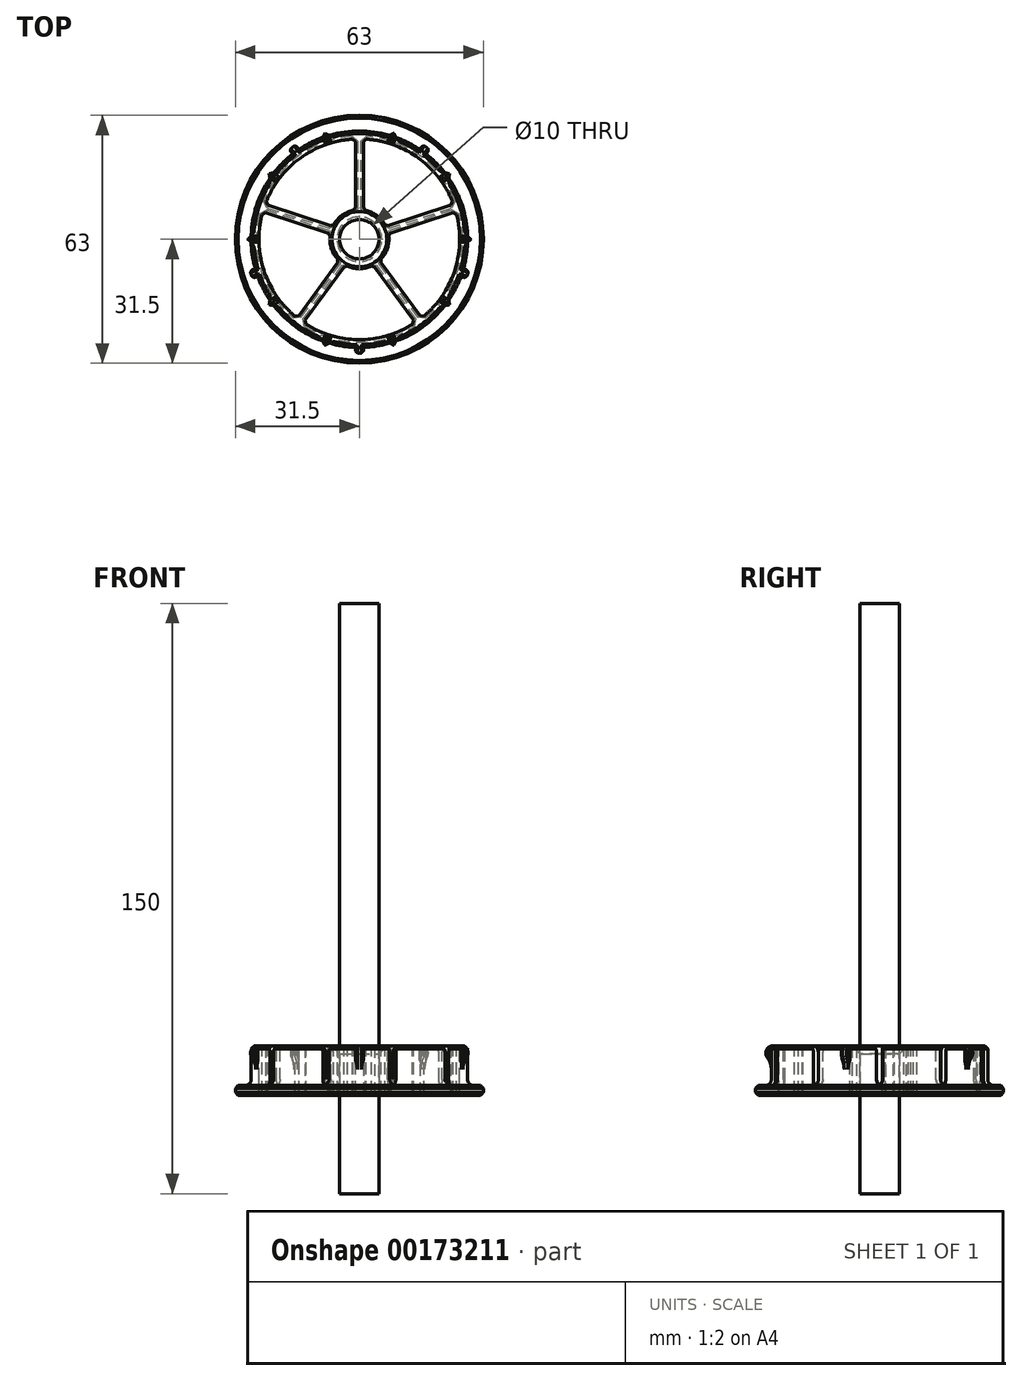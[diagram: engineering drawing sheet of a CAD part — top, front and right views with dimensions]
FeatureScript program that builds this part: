
annotation { "Feature Type Name" : "Feature", "Feature Type Description" : "" }
export const myFeature = defineFeature(function(context is Context, id is Id, definition is map)
    precondition{}
    {
        {
            var Q0;
            Q0=qCreatedBy(makeId("Front.planeOp"),FACE);
            var sketch = newSketch(context, id + "F0", { "sketchPlane" : qUnion([Q0])});
            skLineSegment(sketch, "E0", {"start": v(0, 0) * mm, "end": v(-63, 0) * mm, "construction": true});
            skLineSegment(sketch, "E1", {"start": v(-31.5, 0) * mm, "end": v(-31.5, 2.5) * mm});
            skLineSegment(sketch, "E2", {"start": v(-31.5, 2.5) * mm, "end": v(-27.5, 2.5) * mm});
            skLineSegment(sketch, "E3", {"start": v(-27.5, 2.5) * mm, "end": v(-27.5, 8.9) * mm});
            skLineSegment(sketch, "E4", {"start": v(-31.5, 0) * mm, "end": v(-5, 0) * mm});
            skLineSegment(sketch, "E5", {"start": v(-5, 0) * mm, "end": v(-5, 12.5) * mm});
            skLineSegment(sketch, "E6", {"start": v(-5, 12.5) * mm, "end": v(-27.5, 12.5) * mm});
            skLineSegment(sketch, "E7", {"start": v(0, 0) * mm, "end": v(0, 12.5) * mm, "construction": true});
            skLineSegment(sketch, "E8.0.MirrorCS", {"start": v(5, 0) * mm, "end": v(5, 12.5) * mm});
            skLineSegment(sketch, "E9.0.MirrorCS", {"start": v(5, 12.5) * mm, "end": v(27.5, 12.5) * mm});
            skLineSegment(sketch, "E10.0.MirrorCS", {"start": v(27.5, 2.5) * mm, "end": v(27.5, 12.5) * mm});
            skLineSegment(sketch, "E11.0.MirrorCS", {"start": v(31.5, 0) * mm, "end": v(31.5, 2.5) * mm});
            skLineSegment(sketch, "E12.0.MirrorCS", {"start": v(31.5, 0) * mm, "end": v(5, 0) * mm});
            skLineSegment(sketch, "E13.0.MirrorCS", {"start": v(31.5, 2.5) * mm, "end": v(27.5, 2.5) * mm});
            skArc(sketch, "E14", {"start": v(-27.5, 12.5) * mm, "mid": v(-28.9, 10.7) * mm, "end": v(-27.5, 8.9) * mm});
            skSolve(sketch);
        }
        {
            var Q0;
            Q0=makeQuery(id+"F0.imprint","IMPRINT",FACE,{"disambiguationData":[TD([[makeQuery(id+"F0.imprint","IMPRINT",EDGE,{"derivedFrom":sQuery(id+"F0.wireOp",EDGE,"E1")}),-1.0]])]});
            var Q1;
            Q1=sQuery(id+"F0.wireOp",EDGE,"E7");
            revolve(context, id + "F1", {"entities" : qUnion([Q0]), "axis" : qUnion([Q1]), "revolveType" : RevolveType.FULL});
        }
        {
            var Q0;
            Q0=makeQuery(id+"F1.opRevolve","SWEPT_FACE",FACE,{"disambiguationData":[OSD([sQuery(id+"F0.wireOp",EDGE,"E6")])]});
            var sketch = newSketch(context, id + "F2", { "sketchPlane" : qUnion([Q0])});
            skCircle(sketch, "E15.0", {"center": v(0, 0) * mm, "radius": 31.5 * mm});
            skCircle(sketch, "E15.1", {"center": v(0, 0) * mm, "radius": 5 * mm});
            skCircle(sketch, "E16.0", {"center": v(0, 0) * mm, "radius": 27.5 * mm});
            skCircle(sketch, "E17", {"center": v(0, 0) * mm, "radius": 7.5 * mm});
            skCircle(sketch, "E18", {"center": v(0, 0) * mm, "radius": 25.5 * mm});
            skLineSegment(sketch, "E19", {"start": v(0, 0) * mm, "end": v(0, 31.5) * mm, "construction": true});
            skLineSegment(sketch, "E20", {"start": v(-1, 7.43) * mm, "end": v(-1, 25.48) * mm});
            skLineSegment(sketch, "E21.0.MirrorCS", {"start": v(1, 7.43) * mm, "end": v(1, 25.48) * mm});
            skLineSegment(sketch, "E22.1.0", {"start": v(-7.38, 1.35) * mm, "end": v(-24.54, 6.92) * mm});
            skLineSegment(sketch, "E22.1.1", {"start": v(-6.76, 3.25) * mm, "end": v(-23.92, 8.82) * mm});
            skLineSegment(sketch, "E22.2.0", {"start": v(-3.56, -6.6) * mm, "end": v(-14.17, -21.2) * mm});
            skLineSegment(sketch, "E22.2.1", {"start": v(-5.18, -5.43) * mm, "end": v(-15.79, -20.03) * mm});
            skLineSegment(sketch, "E22.3.0", {"start": v(5.18, -5.43) * mm, "end": v(15.79, -20.03) * mm});
            skLineSegment(sketch, "E22.3.1", {"start": v(3.56, -6.6) * mm, "end": v(14.17, -21.2) * mm});
            skLineSegment(sketch, "E22.4.0", {"start": v(6.76, 3.25) * mm, "end": v(23.92, 8.82) * mm});
            skLineSegment(sketch, "E22.4.1", {"start": v(7.38, 1.35) * mm, "end": v(24.54, 6.92) * mm});
            skLineSegment(sketch, "E23", {"start": v(16.16, 22.25) * mm, "end": v(-16.16, -22.25) * mm, "construction": true});
            skLineSegment(sketch, "E24", {"start": v(15.34, 22.82) * mm, "end": v(17.7, 26.06) * mm});
            skLineSegment(sketch, "E25.0.MirrorCS", {"start": v(16.96, 21.65) * mm, "end": v(19.31, 24.88) * mm});
            skLineSegment(sketch, "E26.1.0", {"start": v(-16.96, 21.65) * mm, "end": v(-19.31, 24.88) * mm});
            skLineSegment(sketch, "E26.1.1", {"start": v(-15.34, 22.82) * mm, "end": v(-17.7, 26.06) * mm});
            skLineSegment(sketch, "E26.2.0", {"start": v(-25.83, -9.44) * mm, "end": v(-29.63, -10.68) * mm});
            skLineSegment(sketch, "E26.2.1", {"start": v(-26.45, -7.54) * mm, "end": v(-30.25, -8.78) * mm});
            skLineSegment(sketch, "E26.3.0", {"start": v(1, -27.48) * mm, "end": v(1, -31.48) * mm});
            skLineSegment(sketch, "E26.3.1", {"start": v(-1, -27.48) * mm, "end": v(-1, -31.48) * mm});
            skLineSegment(sketch, "E26.4.0", {"start": v(26.45, -7.54) * mm, "end": v(30.25, -8.78) * mm});
            skLineSegment(sketch, "E26.4.1", {"start": v(25.83, -9.44) * mm, "end": v(29.63, -10.68) * mm});
            skSolve(sketch);
        }
        {
            var Q0;
            {var subQ10=sQuery(id+"F2.wireOp",EDGE,"E16.0");var subQ16=makeQuery(id+"F2.imprint","INTERSECT",VERTEX,{"derivedFrom":[subQ10,sQuery(id+"F2.wireOp",EDGE,"E26.1.0")]});Q0=makeQuery(id+"F2.imprint","IMPRINT",FACE,{"disambiguationData":[TD([[makeQuery(id+"F2.imprint","IMPRINT",EDGE,{"disambiguationData":[TD([[subQ16,-1.0]])],"derivedFrom":subQ10}),-1.0]])]});}
            var sketch = newSketch(context, id + "F3", { "sketchPlane" : qUnion([Q0])});
            skLineSegment(sketch, "E27.0", {"start": v(0, 0) * mm, "end": v(0, 31.5) * mm, "construction": true});
            skLineSegment(sketch, "E27.1", {"start": v(16.16, 22.25) * mm, "end": v(-16.16, -22.25) * mm, "construction": true});
            skCircle(sketch, "E27.2", {"center": v(0, 0) * mm, "radius": 25.5 * mm});
            skCircle(sketch, "E27.3", {"center": v(0, 0) * mm, "radius": 27.5 * mm});
            skPoint(sketch, "E28", {"position": v(0, 27.5) * mm});
            skLineSegment(sketch, "E29", {"start": v(0, 27.5) * mm, "end": v(8.5, 26.15) * mm, "construction": true});
            skLineSegment(sketch, "E30", {"start": v(8.5, 26.15) * mm, "end": v(16.16, 22.25) * mm, "construction": true});
            skLineSegment(sketch, "E31", {"start": v(0, 0) * mm, "end": v(8.5, 26.15) * mm, "construction": true});
            skLineSegment(sketch, "E32", {"start": v(7.73, 26.4) * mm, "end": v(7.16, 24.47) * mm});
            skLineSegment(sketch, "E33.0.MirrorCS", {"start": v(9.26, 25.9) * mm, "end": v(8.59, 24) * mm});
            skLineSegment(sketch, "E34.1.0", {"start": v(-9.26, 25.9) * mm, "end": v(-8.59, 24) * mm});
            skLineSegment(sketch, "E34.1.1", {"start": v(-7.73, 26.4) * mm, "end": v(-7.16, 24.47) * mm});
            skLineSegment(sketch, "E34.2.0", {"start": v(-22.71, 15.5) * mm, "end": v(-21.06, 14.38) * mm});
            skLineSegment(sketch, "E34.2.1", {"start": v(-21.76, 16.81) * mm, "end": v(-20.18, 15.59) * mm});
            skLineSegment(sketch, "E34.3.0", {"start": v(-27.49, -0.8) * mm, "end": v(-25.49, -0.75) * mm});
            skLineSegment(sketch, "E34.3.1", {"start": v(-27.49, 0.8) * mm, "end": v(-25.49, 0.75) * mm});
            skLineSegment(sketch, "E34.4.0", {"start": v(-21.76, -16.81) * mm, "end": v(-20.18, -15.59) * mm});
            skLineSegment(sketch, "E34.4.1", {"start": v(-22.71, -15.5) * mm, "end": v(-21.06, -14.38) * mm});
            skLineSegment(sketch, "E34.5.0", {"start": v(-7.73, -26.4) * mm, "end": v(-7.16, -24.47) * mm});
            skLineSegment(sketch, "E34.5.1", {"start": v(-9.26, -25.9) * mm, "end": v(-8.59, -24) * mm});
            skLineSegment(sketch, "E34.6.0", {"start": v(9.26, -25.9) * mm, "end": v(8.59, -24) * mm});
            skLineSegment(sketch, "E34.6.1", {"start": v(7.73, -26.4) * mm, "end": v(7.16, -24.47) * mm});
            skLineSegment(sketch, "E34.7.0", {"start": v(22.71, -15.5) * mm, "end": v(21.06, -14.38) * mm});
            skLineSegment(sketch, "E34.7.1", {"start": v(21.76, -16.81) * mm, "end": v(20.18, -15.59) * mm});
            skLineSegment(sketch, "E34.8.0", {"start": v(27.49, 0.8) * mm, "end": v(25.49, 0.75) * mm});
            skLineSegment(sketch, "E34.8.1", {"start": v(27.49, -0.8) * mm, "end": v(25.49, -0.75) * mm});
            skLineSegment(sketch, "E34.9.0", {"start": v(21.76, 16.81) * mm, "end": v(20.18, 15.59) * mm});
            skLineSegment(sketch, "E34.9.1", {"start": v(22.71, 15.5) * mm, "end": v(21.06, 14.38) * mm});
            skSolve(sketch);
        }
        {
            var Q0;
            {var subQ2=sQuery(id+"F2.wireOp",EDGE,"E20");Q0=makeQuery(id+"F2.imprint","IMPRINT",FACE,{"disambiguationData":[TD([[makeQuery(id+"F2.imprint","IMPRINT",EDGE,{"derivedFrom":subQ2}),1.0]])]});}
            var Q1;
            {var subQ1=sQuery(id+"F2.wireOp",EDGE,"E21.0.MirrorCS");Q1=makeQuery(id+"F2.imprint","IMPRINT",FACE,{"disambiguationData":[TD([[makeQuery(id+"F2.imprint","IMPRINT",EDGE,{"derivedFrom":subQ1}),-1.0]])]});}
            var Q2;
            {var subQ1=sQuery(id+"F2.wireOp",EDGE,"E22.3.0");Q2=makeQuery(id+"F2.imprint","IMPRINT",FACE,{"disambiguationData":[TD([[makeQuery(id+"F2.imprint","IMPRINT",EDGE,{"derivedFrom":subQ1}),1.0]])]});}
            var Q3;
            {var subQ2=sQuery(id+"F2.wireOp",EDGE,"E22.2.0");Q3=makeQuery(id+"F2.imprint","IMPRINT",FACE,{"disambiguationData":[TD([[makeQuery(id+"F2.imprint","IMPRINT",EDGE,{"derivedFrom":subQ2}),1.0]])]});}
            var Q4;
            {var subQ1=sQuery(id+"F2.wireOp",EDGE,"E22.1.0");Q4=makeQuery(id+"F2.imprint","IMPRINT",FACE,{"disambiguationData":[TD([[makeQuery(id+"F2.imprint","IMPRINT",EDGE,{"derivedFrom":subQ1}),1.0]])]});}
            var Q5;
            Q5=makeQuery(id+"F1.opRevolve","SWEPT_FACE",FACE,{"disambiguationData":[OSD([sQuery(id+"F0.wireOp",EDGE,"E4")])]});
            extrude(context, id + "F4", {"entities" : qUnion([Q0, Q1, Q2, Q3, Q4]), "operationType" : NewBodyOperationType.REMOVE, "endBound" : BoundingType.UP_TO_SURFACE, "oppositeDirection" : true, "endBoundEntityFace" : qUnion([Q5]), "depth" : 25 * mm});
        }
        {
            var Q0;
            {var subQ0=sQuery(id+"F2.wireOp",EDGE,"E24");Q0=makeQuery(id+"F2.imprint","IMPRINT",FACE,{"disambiguationData":[TD([[makeQuery(id+"F2.imprint","IMPRINT",EDGE,{"derivedFrom":subQ0}),1.0]])]});}
            var Q1;
            {var subQ1=sQuery(id+"F2.wireOp",EDGE,"E25.0.MirrorCS");Q1=makeQuery(id+"F2.imprint","IMPRINT",FACE,{"disambiguationData":[TD([[makeQuery(id+"F2.imprint","IMPRINT",EDGE,{"derivedFrom":subQ1}),-1.0]])]});}
            var Q2;
            {var subQ1=sQuery(id+"F2.wireOp",EDGE,"E26.3.0");Q2=makeQuery(id+"F2.imprint","IMPRINT",FACE,{"disambiguationData":[TD([[makeQuery(id+"F2.imprint","IMPRINT",EDGE,{"derivedFrom":subQ1}),1.0]])]});}
            var Q3;
            {var subQ1=sQuery(id+"F2.wireOp",EDGE,"E26.2.0");Q3=makeQuery(id+"F2.imprint","IMPRINT",FACE,{"disambiguationData":[TD([[makeQuery(id+"F2.imprint","IMPRINT",EDGE,{"derivedFrom":subQ1}),1.0]])]});}
            var Q4;
            {var subQ1=sQuery(id+"F2.wireOp",EDGE,"E26.1.0");Q4=makeQuery(id+"F2.imprint","IMPRINT",FACE,{"disambiguationData":[TD([[makeQuery(id+"F2.imprint","IMPRINT",EDGE,{"derivedFrom":subQ1}),1.0]])]});}
            extrude(context, id + "F5", {"entities" : qUnion([Q0, Q1, Q2, Q3, Q4]), "operationType" : NewBodyOperationType.REMOVE, "endBound" : BoundingType.UP_TO_NEXT, "oppositeDirection" : true, "depth" : 25 * mm});
        }
        {
            var Q0;
            {var subQ1=sQuery(id+"F3.wireOp",EDGE,"E34.1.0");Q0=makeQuery(id+"F3.imprint","IMPRINT",FACE,{"disambiguationData":[TD([[makeQuery(id+"F3.imprint","IMPRINT",EDGE,{"derivedFrom":subQ1}),1.0]])]});}
            var Q1;
            {var subQ1=sQuery(id+"F3.wireOp",EDGE,"E34.2.0");Q1=makeQuery(id+"F3.imprint","IMPRINT",FACE,{"disambiguationData":[TD([[makeQuery(id+"F3.imprint","IMPRINT",EDGE,{"derivedFrom":subQ1}),1.0]])]});}
            var Q2;
            {var subQ1=sQuery(id+"F3.wireOp",EDGE,"E34.3.0");Q2=makeQuery(id+"F3.imprint","IMPRINT",FACE,{"disambiguationData":[TD([[makeQuery(id+"F3.imprint","IMPRINT",EDGE,{"derivedFrom":subQ1}),1.0]])]});}
            var Q3;
            {var subQ1=sQuery(id+"F3.wireOp",EDGE,"E34.4.0");Q3=makeQuery(id+"F3.imprint","IMPRINT",FACE,{"disambiguationData":[TD([[makeQuery(id+"F3.imprint","IMPRINT",EDGE,{"derivedFrom":subQ1}),1.0]])]});}
            var Q4;
            {var subQ1=sQuery(id+"F3.wireOp",EDGE,"E34.5.0");Q4=makeQuery(id+"F3.imprint","IMPRINT",FACE,{"disambiguationData":[TD([[makeQuery(id+"F3.imprint","IMPRINT",EDGE,{"derivedFrom":subQ1}),1.0]])]});}
            var Q5;
            {var subQ1=sQuery(id+"F3.wireOp",EDGE,"E34.6.0");Q5=makeQuery(id+"F3.imprint","IMPRINT",FACE,{"disambiguationData":[TD([[makeQuery(id+"F3.imprint","IMPRINT",EDGE,{"derivedFrom":subQ1}),1.0]])]});}
            var Q6;
            {var subQ1=sQuery(id+"F3.wireOp",EDGE,"E34.7.0");Q6=makeQuery(id+"F3.imprint","IMPRINT",FACE,{"disambiguationData":[TD([[makeQuery(id+"F3.imprint","IMPRINT",EDGE,{"derivedFrom":subQ1}),1.0]])]});}
            var Q7;
            {var subQ1=sQuery(id+"F3.wireOp",EDGE,"E34.8.0");Q7=makeQuery(id+"F3.imprint","IMPRINT",FACE,{"disambiguationData":[TD([[makeQuery(id+"F3.imprint","IMPRINT",EDGE,{"derivedFrom":subQ1}),1.0]])]});}
            var Q8;
            {var subQ1=sQuery(id+"F3.wireOp",EDGE,"E34.9.0");Q8=makeQuery(id+"F3.imprint","IMPRINT",FACE,{"disambiguationData":[TD([[makeQuery(id+"F3.imprint","IMPRINT",EDGE,{"derivedFrom":subQ1}),1.0]])]});}
            var Q9;
            {var subQ1=sQuery(id+"F3.wireOp",EDGE,"E32");Q9=makeQuery(id+"F3.imprint","IMPRINT",FACE,{"disambiguationData":[TD([[makeQuery(id+"F3.imprint","IMPRINT",EDGE,{"derivedFrom":subQ1}),1.0]])]});}
            var Q10;
            Q10=makeQuery(id+"F1.opRevolve","SWEPT_FACE",FACE,{"disambiguationData":[OSD([sQuery(id+"F0.wireOp",EDGE,"E2")])]});
            extrude(context, id + "F6", {"entities" : qUnion([Q0, Q1, Q2, Q3, Q4, Q5, Q6, Q7, Q8, Q9]), "operationType" : NewBodyOperationType.REMOVE, "endBound" : BoundingType.UP_TO_SURFACE, "oppositeDirection" : true, "endBoundEntityFace" : qUnion([Q10]), "depth" : 10 * mm});
        }
        {
            var Q0;
            {var subQ0=sQuery(id+"F0.wireOp",EDGE,"E6");var subQ1=sQuery(id+"F0.wireOp",EDGE,"E14");var subQ2=makeQuery(id+"F1.opRevolve","SWEPT_EDGE",EDGE,{"disambiguationData":[OSD([subQ0,subQ1])]});var subQ3=sQuery(id+"F2.wireOp",EDGE,"E16.0");Q0=makeQuery(id+"F5.boolean.opBoolean","MERGE",EDGE,{"derivedFrom":[subQ2,makeQuery(id+"F5.opExtrude","CAP_EDGE",EDGE,{"disambiguationData":[OSD([subQ0,subQ1,subQ3]),TDD([subQ2,makeQuery(id+"F2.imprint","IMPRINT",EDGE,{"disambiguationData":[TD([[makeQuery(id+"F2.imprint","INTERSECT",VERTEX,{"derivedFrom":[subQ3,sQuery(id+"F2.wireOp",EDGE,"E26.1.0")]}),1.0]])],"derivedFrom":subQ3})])],"isStart":true})]});}
            var Q1;
            {var subQ0=sQuery(id+"F0.wireOp",EDGE,"E6");var subQ1=sQuery(id+"F0.wireOp",EDGE,"E14");var subQ2=makeQuery(id+"F1.opRevolve","SWEPT_EDGE",EDGE,{"disambiguationData":[OSD([subQ0,subQ1])]});var subQ3=sQuery(id+"F2.wireOp",EDGE,"E16.0");Q1=makeQuery(id+"F5.boolean.opBoolean","MERGE",EDGE,{"derivedFrom":[subQ2,makeQuery(id+"F5.opExtrude","CAP_EDGE",EDGE,{"disambiguationData":[OSD([subQ0,subQ1,subQ3]),TDD([subQ2,makeQuery(id+"F2.imprint","IMPRINT",EDGE,{"disambiguationData":[TD([[makeQuery(id+"F2.imprint","INTERSECT",VERTEX,{"derivedFrom":[subQ3,sQuery(id+"F2.wireOp",EDGE,"E26.2.0")]}),1.0]])],"derivedFrom":subQ3})])],"isStart":true})]});}
            var Q2;
            {var subQ0=sQuery(id+"F0.wireOp",EDGE,"E6");var subQ1=sQuery(id+"F0.wireOp",EDGE,"E14");var subQ2=makeQuery(id+"F1.opRevolve","SWEPT_EDGE",EDGE,{"disambiguationData":[OSD([subQ0,subQ1])]});var subQ3=sQuery(id+"F2.wireOp",EDGE,"E16.0");Q2=makeQuery(id+"F5.boolean.opBoolean","MERGE",EDGE,{"derivedFrom":[subQ2,makeQuery(id+"F5.opExtrude","CAP_EDGE",EDGE,{"disambiguationData":[OSD([subQ0,subQ1,subQ3]),TDD([subQ2,makeQuery(id+"F2.imprint","IMPRINT",EDGE,{"disambiguationData":[TD([[makeQuery(id+"F2.imprint","INTERSECT",VERTEX,{"derivedFrom":[subQ3,sQuery(id+"F2.wireOp",EDGE,"E26.3.0")]}),1.0]])],"derivedFrom":subQ3})])],"isStart":true})]});}
            var Q3;
            {var subQ0=sQuery(id+"F0.wireOp",EDGE,"E6");var subQ1=sQuery(id+"F0.wireOp",EDGE,"E14");var subQ2=makeQuery(id+"F1.opRevolve","SWEPT_EDGE",EDGE,{"disambiguationData":[OSD([subQ0,subQ1])]});var subQ3=sQuery(id+"F2.wireOp",EDGE,"E16.0");Q3=makeQuery(id+"F5.boolean.opBoolean","MERGE",EDGE,{"derivedFrom":[subQ2,makeQuery(id+"F5.opExtrude","CAP_EDGE",EDGE,{"disambiguationData":[OSD([subQ0,subQ1,subQ3]),TDD([subQ2,makeQuery(id+"F2.imprint","IMPRINT",EDGE,{"disambiguationData":[TD([[makeQuery(id+"F2.imprint","INTERSECT",VERTEX,{"derivedFrom":[subQ3,sQuery(id+"F2.wireOp",EDGE,"E25.0.MirrorCS")]}),-1.0]])],"derivedFrom":subQ3})])],"isStart":true})]});}
            var Q4;
            {var subQ0=sQuery(id+"F0.wireOp",EDGE,"E6");var subQ1=sQuery(id+"F0.wireOp",EDGE,"E14");var subQ2=makeQuery(id+"F1.opRevolve","SWEPT_EDGE",EDGE,{"disambiguationData":[OSD([subQ0,subQ1])]});var subQ3=sQuery(id+"F2.wireOp",EDGE,"E16.0");Q4=makeQuery(id+"F5.boolean.opBoolean","MERGE",EDGE,{"derivedFrom":[subQ2,makeQuery(id+"F5.opExtrude","CAP_EDGE",EDGE,{"disambiguationData":[OSD([subQ0,subQ1,subQ3]),TDD([subQ2,makeQuery(id+"F2.imprint","IMPRINT",EDGE,{"disambiguationData":[TD([[makeQuery(id+"F2.imprint","INTERSECT",VERTEX,{"derivedFrom":[subQ3,sQuery(id+"F2.wireOp",EDGE,"E24")]}),1.0]])],"derivedFrom":subQ3})])],"isStart":true})]});}
            var Q5;
            {var subQ0=sQuery(id+"F2.wireOp",EDGE,"E18");Q5=makeQuery(id+"F4.boolean.opBoolean","COPY",EDGE,{"derivedFrom":makeQuery(id+"F4.opExtrude","CAP_EDGE",EDGE,{"disambiguationData":[OSD([subQ0]),TDD([makeQuery(id+"F2.imprint","IMPRINT",EDGE,{"disambiguationData":[TD([[makeQuery(id+"F2.imprint","INTERSECT",VERTEX,{"derivedFrom":[subQ0,sQuery(id+"F2.wireOp",EDGE,"E20")]}),-1.0]])],"derivedFrom":subQ0})])],"isStart":true})});}
            var Q6;
            Q6=makeQuery(id+"F4.boolean.opBoolean","COPY",EDGE,{"derivedFrom":makeQuery(id+"F4.opExtrude","CAP_EDGE",EDGE,{"disambiguationData":[OSD([sQuery(id+"F2.wireOp",EDGE,"E22.1.1")])],"isStart":true})});
            var Q7;
            {var subQ0=sQuery(id+"F2.wireOp",EDGE,"E17");Q7=makeQuery(id+"F4.boolean.opBoolean","COPY",EDGE,{"derivedFrom":makeQuery(id+"F4.opExtrude","CAP_EDGE",EDGE,{"disambiguationData":[OSD([subQ0]),TDD([makeQuery(id+"F2.imprint","IMPRINT",EDGE,{"disambiguationData":[TD([[makeQuery(id+"F2.imprint","INTERSECT",VERTEX,{"derivedFrom":[subQ0,sQuery(id+"F2.wireOp",EDGE,"E20")]}),-1.0]])],"derivedFrom":subQ0})])],"isStart":true})});}
            var Q8;
            Q8=makeQuery(id+"F4.boolean.opBoolean","COPY",EDGE,{"derivedFrom":makeQuery(id+"F4.opExtrude","CAP_EDGE",EDGE,{"disambiguationData":[OSD([sQuery(id+"F2.wireOp",EDGE,"E20")])],"isStart":true})});
            var Q9;
            Q9=makeQuery(id+"F4.boolean.opBoolean","COPY",EDGE,{"derivedFrom":makeQuery(id+"F4.opExtrude","CAP_EDGE",EDGE,{"disambiguationData":[OSD([sQuery(id+"F2.wireOp",EDGE,"E22.1.0")])],"isStart":true})});
            var Q10;
            {var subQ0=sQuery(id+"F2.wireOp",EDGE,"E18");Q10=makeQuery(id+"F4.boolean.opBoolean","COPY",EDGE,{"derivedFrom":makeQuery(id+"F4.opExtrude","CAP_EDGE",EDGE,{"disambiguationData":[OSD([subQ0]),TDD([makeQuery(id+"F2.imprint","IMPRINT",EDGE,{"disambiguationData":[TD([[makeQuery(id+"F2.imprint","INTERSECT",VERTEX,{"derivedFrom":[subQ0,sQuery(id+"F2.wireOp",EDGE,"E22.1.0")]}),-1.0]])],"derivedFrom":subQ0})])],"isStart":true})});}
            var Q11;
            Q11=makeQuery(id+"F4.boolean.opBoolean","COPY",EDGE,{"derivedFrom":makeQuery(id+"F4.opExtrude","CAP_EDGE",EDGE,{"disambiguationData":[OSD([sQuery(id+"F2.wireOp",EDGE,"E22.2.1")])],"isStart":true})});
            var Q12;
            {var subQ0=sQuery(id+"F2.wireOp",EDGE,"E17");Q12=makeQuery(id+"F4.boolean.opBoolean","COPY",EDGE,{"derivedFrom":makeQuery(id+"F4.opExtrude","CAP_EDGE",EDGE,{"disambiguationData":[OSD([subQ0]),TDD([makeQuery(id+"F2.imprint","IMPRINT",EDGE,{"disambiguationData":[TD([[makeQuery(id+"F2.imprint","INTERSECT",VERTEX,{"derivedFrom":[subQ0,sQuery(id+"F2.wireOp",EDGE,"E22.1.0")]}),-1.0]])],"derivedFrom":subQ0})])],"isStart":true})});}
            var Q13;
            Q13=makeQuery(id+"F4.boolean.opBoolean","COPY",EDGE,{"derivedFrom":makeQuery(id+"F4.opExtrude","CAP_EDGE",EDGE,{"disambiguationData":[OSD([sQuery(id+"F2.wireOp",EDGE,"E22.2.0")])],"isStart":true})});
            var Q14;
            {var subQ0=sQuery(id+"F2.wireOp",EDGE,"E18");Q14=makeQuery(id+"F4.boolean.opBoolean","COPY",EDGE,{"derivedFrom":makeQuery(id+"F4.opExtrude","CAP_EDGE",EDGE,{"disambiguationData":[OSD([subQ0]),TDD([makeQuery(id+"F2.imprint","IMPRINT",EDGE,{"disambiguationData":[TD([[makeQuery(id+"F2.imprint","INTERSECT",VERTEX,{"derivedFrom":[subQ0,sQuery(id+"F2.wireOp",EDGE,"E22.2.0")]}),-1.0]])],"derivedFrom":subQ0})])],"isStart":true})});}
            var Q15;
            {var subQ0=sQuery(id+"F2.wireOp",EDGE,"E17");Q15=makeQuery(id+"F4.boolean.opBoolean","COPY",EDGE,{"derivedFrom":makeQuery(id+"F4.opExtrude","CAP_EDGE",EDGE,{"disambiguationData":[OSD([subQ0]),TDD([makeQuery(id+"F2.imprint","IMPRINT",EDGE,{"disambiguationData":[TD([[makeQuery(id+"F2.imprint","INTERSECT",VERTEX,{"derivedFrom":[subQ0,sQuery(id+"F2.wireOp",EDGE,"E22.2.0")]}),-1.0]])],"derivedFrom":subQ0})])],"isStart":true})});}
            var Q16;
            Q16=makeQuery(id+"F4.boolean.opBoolean","COPY",EDGE,{"derivedFrom":makeQuery(id+"F4.opExtrude","CAP_EDGE",EDGE,{"disambiguationData":[OSD([sQuery(id+"F2.wireOp",EDGE,"E22.3.1")])],"isStart":true})});
            var Q17;
            Q17=makeQuery(id+"F4.boolean.opBoolean","COPY",EDGE,{"derivedFrom":makeQuery(id+"F4.opExtrude","CAP_EDGE",EDGE,{"disambiguationData":[OSD([sQuery(id+"F2.wireOp",EDGE,"E22.3.0")])],"isStart":true})});
            var Q18;
            {var subQ0=sQuery(id+"F2.wireOp",EDGE,"E17");Q18=makeQuery(id+"F4.boolean.opBoolean","COPY",EDGE,{"derivedFrom":makeQuery(id+"F4.opExtrude","CAP_EDGE",EDGE,{"disambiguationData":[OSD([subQ0]),TDD([makeQuery(id+"F2.imprint","IMPRINT",EDGE,{"disambiguationData":[TD([[makeQuery(id+"F2.imprint","INTERSECT",VERTEX,{"derivedFrom":[subQ0,sQuery(id+"F2.wireOp",EDGE,"E22.3.0")]}),-1.0]])],"derivedFrom":subQ0})])],"isStart":true})});}
            var Q19;
            {var subQ0=sQuery(id+"F2.wireOp",EDGE,"E18");Q19=makeQuery(id+"F4.boolean.opBoolean","COPY",EDGE,{"derivedFrom":makeQuery(id+"F4.opExtrude","CAP_EDGE",EDGE,{"disambiguationData":[OSD([subQ0]),TDD([makeQuery(id+"F2.imprint","IMPRINT",EDGE,{"disambiguationData":[TD([[makeQuery(id+"F2.imprint","INTERSECT",VERTEX,{"derivedFrom":[subQ0,sQuery(id+"F2.wireOp",EDGE,"E22.3.0")]}),-1.0]])],"derivedFrom":subQ0})])],"isStart":true})});}
            var Q20;
            Q20=makeQuery(id+"F4.boolean.opBoolean","COPY",EDGE,{"derivedFrom":makeQuery(id+"F4.opExtrude","CAP_EDGE",EDGE,{"disambiguationData":[OSD([sQuery(id+"F2.wireOp",EDGE,"E22.4.1")])],"isStart":true})});
            var Q21;
            Q21=makeQuery(id+"F4.boolean.opBoolean","COPY",EDGE,{"derivedFrom":makeQuery(id+"F4.opExtrude","CAP_EDGE",EDGE,{"disambiguationData":[OSD([sQuery(id+"F2.wireOp",EDGE,"E22.4.0")])],"isStart":true})});
            var Q22;
            {var subQ0=sQuery(id+"F2.wireOp",EDGE,"E17");Q22=makeQuery(id+"F4.boolean.opBoolean","COPY",EDGE,{"derivedFrom":makeQuery(id+"F4.opExtrude","CAP_EDGE",EDGE,{"disambiguationData":[OSD([subQ0]),TDD([makeQuery(id+"F2.imprint","IMPRINT",EDGE,{"disambiguationData":[TD([[makeQuery(id+"F2.imprint","INTERSECT",VERTEX,{"derivedFrom":[subQ0,sQuery(id+"F2.wireOp",EDGE,"E21.0.MirrorCS")]}),1.0]])],"derivedFrom":subQ0})])],"isStart":true})});}
            var Q23;
            {var subQ0=sQuery(id+"F2.wireOp",EDGE,"E18");Q23=makeQuery(id+"F4.boolean.opBoolean","COPY",EDGE,{"derivedFrom":makeQuery(id+"F4.opExtrude","CAP_EDGE",EDGE,{"disambiguationData":[OSD([subQ0]),TDD([makeQuery(id+"F2.imprint","IMPRINT",EDGE,{"disambiguationData":[TD([[makeQuery(id+"F2.imprint","INTERSECT",VERTEX,{"derivedFrom":[subQ0,sQuery(id+"F2.wireOp",EDGE,"E21.0.MirrorCS")]}),1.0]])],"derivedFrom":subQ0})])],"isStart":true})});}
            var Q24;
            Q24=makeQuery(id+"F4.boolean.opBoolean","COPY",EDGE,{"derivedFrom":makeQuery(id+"F4.opExtrude","CAP_EDGE",EDGE,{"disambiguationData":[OSD([sQuery(id+"F2.wireOp",EDGE,"E21.0.MirrorCS")])],"isStart":true})});
            var Q25;
            Q25=makeQuery(id+"F1.opRevolve","SWEPT_EDGE",EDGE,{"disambiguationData":[OSD([sQuery(id+"F0.wireOp",EDGE,"E1"),sQuery(id+"F0.wireOp",EDGE,"E2")])]});
            var Q26;
            Q26=makeQuery(id+"F1.opRevolve","SWEPT_EDGE",EDGE,{"disambiguationData":[OSD([sQuery(id+"F0.wireOp",EDGE,"E1"),sQuery(id+"F0.wireOp",EDGE,"E4")])]});
            var Q27;
            Q27=makeQuery(id+"F4.boolean.opBoolean","COPY",EDGE,{"derivedFrom":makeQuery(id+"F4.opExtrude","SWEPT_EDGE",EDGE,{"disambiguationData":[OSD([sQuery(id+"F2.wireOp",EDGE,"E18"),sQuery(id+"F2.wireOp",EDGE,"E22.4.0")])]})});
            var Q28;
            Q28=makeQuery(id+"F4.boolean.opBoolean","COPY",EDGE,{"derivedFrom":makeQuery(id+"F4.opExtrude","SWEPT_EDGE",EDGE,{"disambiguationData":[OSD([sQuery(id+"F2.wireOp",EDGE,"E18"),sQuery(id+"F2.wireOp",EDGE,"E22.4.1")])]})});
            var Q29;
            Q29=makeQuery(id+"F4.boolean.opBoolean","COPY",EDGE,{"derivedFrom":makeQuery(id+"F4.opExtrude","SWEPT_EDGE",EDGE,{"disambiguationData":[OSD([sQuery(id+"F2.wireOp",EDGE,"E18"),sQuery(id+"F2.wireOp",EDGE,"E22.3.0")])]})});
            var Q30;
            Q30=makeQuery(id+"F4.boolean.opBoolean","COPY",EDGE,{"derivedFrom":makeQuery(id+"F4.opExtrude","SWEPT_EDGE",EDGE,{"disambiguationData":[OSD([sQuery(id+"F2.wireOp",EDGE,"E18"),sQuery(id+"F2.wireOp",EDGE,"E22.3.1")])]})});
            var Q31;
            Q31=makeQuery(id+"F4.boolean.opBoolean","COPY",EDGE,{"derivedFrom":makeQuery(id+"F4.opExtrude","SWEPT_EDGE",EDGE,{"disambiguationData":[OSD([sQuery(id+"F2.wireOp",EDGE,"E18"),sQuery(id+"F2.wireOp",EDGE,"E22.2.0")])]})});
            var Q32;
            Q32=makeQuery(id+"F4.boolean.opBoolean","COPY",EDGE,{"derivedFrom":makeQuery(id+"F4.opExtrude","SWEPT_EDGE",EDGE,{"disambiguationData":[OSD([sQuery(id+"F2.wireOp",EDGE,"E18"),sQuery(id+"F2.wireOp",EDGE,"E22.2.1")])]})});
            var Q33;
            Q33=makeQuery(id+"F4.boolean.opBoolean","COPY",EDGE,{"derivedFrom":makeQuery(id+"F4.opExtrude","SWEPT_EDGE",EDGE,{"disambiguationData":[OSD([sQuery(id+"F2.wireOp",EDGE,"E17"),sQuery(id+"F2.wireOp",EDGE,"E22.1.0")])]})});
            var Q34;
            Q34=makeQuery(id+"F4.boolean.opBoolean","COPY",EDGE,{"derivedFrom":makeQuery(id+"F4.opExtrude","SWEPT_EDGE",EDGE,{"disambiguationData":[OSD([sQuery(id+"F2.wireOp",EDGE,"E17"),sQuery(id+"F2.wireOp",EDGE,"E22.1.1")])]})});
            var Q35;
            Q35=makeQuery(id+"F4.boolean.opBoolean","COPY",EDGE,{"derivedFrom":makeQuery(id+"F4.opExtrude","SWEPT_EDGE",EDGE,{"disambiguationData":[OSD([sQuery(id+"F2.wireOp",EDGE,"E17"),sQuery(id+"F2.wireOp",EDGE,"E20")])]})});
            var Q36;
            Q36=makeQuery(id+"F4.boolean.opBoolean","COPY",EDGE,{"derivedFrom":makeQuery(id+"F4.opExtrude","SWEPT_EDGE",EDGE,{"disambiguationData":[OSD([sQuery(id+"F2.wireOp",EDGE,"E17"),sQuery(id+"F2.wireOp",EDGE,"E21.0.MirrorCS")])]})});
            var Q37;
            Q37=makeQuery(id+"F4.boolean.opBoolean","COPY",EDGE,{"derivedFrom":makeQuery(id+"F4.opExtrude","SWEPT_EDGE",EDGE,{"disambiguationData":[OSD([sQuery(id+"F2.wireOp",EDGE,"E17"),sQuery(id+"F2.wireOp",EDGE,"E22.4.0")])]})});
            var Q38;
            Q38=makeQuery(id+"F4.boolean.opBoolean","COPY",EDGE,{"derivedFrom":makeQuery(id+"F4.opExtrude","SWEPT_EDGE",EDGE,{"disambiguationData":[OSD([sQuery(id+"F2.wireOp",EDGE,"E17"),sQuery(id+"F2.wireOp",EDGE,"E22.4.1")])]})});
            var Q39;
            Q39=makeQuery(id+"F4.boolean.opBoolean","COPY",EDGE,{"derivedFrom":makeQuery(id+"F4.opExtrude","SWEPT_EDGE",EDGE,{"disambiguationData":[OSD([sQuery(id+"F2.wireOp",EDGE,"E18"),sQuery(id+"F2.wireOp",EDGE,"E21.0.MirrorCS")])]})});
            var Q40;
            Q40=makeQuery(id+"F4.boolean.opBoolean","COPY",EDGE,{"derivedFrom":makeQuery(id+"F4.opExtrude","SWEPT_EDGE",EDGE,{"disambiguationData":[OSD([sQuery(id+"F2.wireOp",EDGE,"E18"),sQuery(id+"F2.wireOp",EDGE,"E20")])]})});
            var Q41;
            Q41=makeQuery(id+"F4.boolean.opBoolean","COPY",EDGE,{"derivedFrom":makeQuery(id+"F4.opExtrude","SWEPT_EDGE",EDGE,{"disambiguationData":[OSD([sQuery(id+"F2.wireOp",EDGE,"E18"),sQuery(id+"F2.wireOp",EDGE,"E22.1.0")])]})});
            var Q42;
            Q42=makeQuery(id+"F4.boolean.opBoolean","COPY",EDGE,{"derivedFrom":makeQuery(id+"F4.opExtrude","SWEPT_EDGE",EDGE,{"disambiguationData":[OSD([sQuery(id+"F2.wireOp",EDGE,"E18"),sQuery(id+"F2.wireOp",EDGE,"E22.1.1")])]})});
            var Q43;
            Q43=makeQuery(id+"F4.boolean.opBoolean","COPY",EDGE,{"derivedFrom":makeQuery(id+"F4.opExtrude","SWEPT_EDGE",EDGE,{"disambiguationData":[OSD([sQuery(id+"F2.wireOp",EDGE,"E17"),sQuery(id+"F2.wireOp",EDGE,"E22.3.1")])]})});
            var Q44;
            Q44=makeQuery(id+"F4.boolean.opBoolean","COPY",EDGE,{"derivedFrom":makeQuery(id+"F4.opExtrude","SWEPT_EDGE",EDGE,{"disambiguationData":[OSD([sQuery(id+"F2.wireOp",EDGE,"E17"),sQuery(id+"F2.wireOp",EDGE,"E22.2.0")])]})});
            var Q45;
            Q45=makeQuery(id+"F4.boolean.opBoolean","COPY",EDGE,{"derivedFrom":makeQuery(id+"F4.opExtrude","SWEPT_EDGE",EDGE,{"disambiguationData":[OSD([sQuery(id+"F2.wireOp",EDGE,"E17"),sQuery(id+"F2.wireOp",EDGE,"E22.2.1")])]})});
            var Q46;
            Q46=makeQuery(id+"F4.boolean.opBoolean","COPY",EDGE,{"derivedFrom":makeQuery(id+"F4.opExtrude","SWEPT_EDGE",EDGE,{"disambiguationData":[OSD([sQuery(id+"F2.wireOp",EDGE,"E17"),sQuery(id+"F2.wireOp",EDGE,"E22.3.0")])]})});
            var Q47;
            Q47=makeQuery(id+"F1.opRevolve","SWEPT_FACE",FACE,{"disambiguationData":[OSD([sQuery(id+"F0.wireOp",EDGE,"E4")])]});
            chamfer(context, id + "F7", {"entities" : qUnion([Q0, Q1, Q2, Q3, Q4, Q5, Q6, Q7, Q8, Q9, Q10, Q11, Q12, Q13, Q14, Q15, Q16, Q17, Q18, Q19, Q20, Q21, Q22, Q23, Q24, Q25, Q26, Q27, Q28, Q29, Q30, Q31, Q32, Q33, Q34, Q35, Q36, Q37, Q38, Q39, Q40, Q41, Q42, Q43, Q44, Q45, Q46, Q47]), "width" : 0.7 * mm, "tangentPropagation" : true});
        }
        {
            var Q0;
            Q0=makeQuery(id+"F1.opRevolve","SWEPT_EDGE",EDGE,{"disambiguationData":[OSD([sQuery(id+"F0.wireOp",EDGE,"E5"),sQuery(id+"F0.wireOp",EDGE,"E6")])]});
            chamfer(context, id + "F8", {"entities" : qUnion([Q0]), "width" : 2 * mm, "tangentPropagation" : true});
        }
        {
            var Q0;
            {var subQ0=sQuery(id+"F0.wireOp",EDGE,"E3");var subQ1=sQuery(id+"F0.wireOp",EDGE,"E14");var subQ3=sQuery(id+"F2.wireOp",EDGE,"E26.4.0");Q0=makeQuery(id+"F5.boolean.opBoolean","SPLIT",EDGE,{"disambiguationData":[TD([makeQuery(id+"F5.opExtrude","SWEPT_FACE",FACE,{"disambiguationData":[OSD([subQ3])]})])],"derivedFrom":makeQuery(id+"F1.opRevolve","SWEPT_EDGE",EDGE,{"disambiguationData":[OSD([subQ0,subQ1])]})});}
            var Q1;
            {var subQ0=sQuery(id+"F0.wireOp",EDGE,"E3");var subQ1=sQuery(id+"F0.wireOp",EDGE,"E14");var subQ3=sQuery(id+"F2.wireOp",EDGE,"E24");Q1=makeQuery(id+"F5.boolean.opBoolean","SPLIT",EDGE,{"disambiguationData":[TD([makeQuery(id+"F5.opExtrude","SWEPT_FACE",FACE,{"disambiguationData":[OSD([subQ3])]})])],"derivedFrom":makeQuery(id+"F1.opRevolve","SWEPT_EDGE",EDGE,{"disambiguationData":[OSD([subQ0,subQ1])]})});}
            var Q2;
            {var subQ0=sQuery(id+"F0.wireOp",EDGE,"E3");var subQ1=sQuery(id+"F0.wireOp",EDGE,"E14");var subQ2=sQuery(id+"F2.wireOp",EDGE,"E26.1.0");Q2=makeQuery(id+"F5.boolean.opBoolean","SPLIT",EDGE,{"disambiguationData":[TD([makeQuery(id+"F5.opExtrude","SWEPT_FACE",FACE,{"disambiguationData":[OSD([subQ2])]})])],"derivedFrom":makeQuery(id+"F1.opRevolve","SWEPT_EDGE",EDGE,{"disambiguationData":[OSD([subQ0,subQ1])]})});}
            var Q3;
            {var subQ0=sQuery(id+"F0.wireOp",EDGE,"E3");var subQ1=sQuery(id+"F0.wireOp",EDGE,"E14");var subQ3=sQuery(id+"F2.wireOp",EDGE,"E26.2.0");Q3=makeQuery(id+"F5.boolean.opBoolean","SPLIT",EDGE,{"disambiguationData":[TD([makeQuery(id+"F5.opExtrude","SWEPT_FACE",FACE,{"disambiguationData":[OSD([subQ3])]})])],"derivedFrom":makeQuery(id+"F1.opRevolve","SWEPT_EDGE",EDGE,{"disambiguationData":[OSD([subQ0,subQ1])]})});}
            var Q4;
            {var subQ0=sQuery(id+"F0.wireOp",EDGE,"E3");var subQ1=sQuery(id+"F0.wireOp",EDGE,"E14");var subQ2=sQuery(id+"F2.wireOp",EDGE,"E26.3.0");Q4=makeQuery(id+"F5.boolean.opBoolean","SPLIT",EDGE,{"disambiguationData":[TD([makeQuery(id+"F5.opExtrude","SWEPT_FACE",FACE,{"disambiguationData":[OSD([subQ2])]})])],"derivedFrom":makeQuery(id+"F1.opRevolve","SWEPT_EDGE",EDGE,{"disambiguationData":[OSD([subQ0,subQ1])]})});}
            fillet(context, id + "F9", {"entities" : qUnion([Q0, Q1, Q2, Q3, Q4]), "radius" : 5 * mm, "tangentPropagation" : true, "allowEdgeOverflow" : false});
        }
        {
            var Q0;
            Q0=makeQuery(id+"F5.boolean.opBoolean","INTERSECT",EDGE,{"derivedFrom":[makeQuery(id+"F1.opRevolve","SWEPT_FACE",FACE,{"disambiguationData":[OSD([sQuery(id+"F0.wireOp",EDGE,"E14")])]}),makeQuery(id+"F5.opExtrude","SWEPT_FACE",FACE,{"disambiguationData":[OSD([sQuery(id+"F2.wireOp",EDGE,"E26.1.0")])]})]});
            var Q1;
            Q1=makeQuery(id+"F5.boolean.opBoolean","INTERSECT",EDGE,{"derivedFrom":[makeQuery(id+"F1.opRevolve","SWEPT_FACE",FACE,{"disambiguationData":[OSD([sQuery(id+"F0.wireOp",EDGE,"E14")])]}),makeQuery(id+"F5.opExtrude","SWEPT_FACE",FACE,{"disambiguationData":[OSD([sQuery(id+"F2.wireOp",EDGE,"E26.1.1")])]})]});
            var Q2;
            Q2=makeQuery(id+"F5.boolean.opBoolean","INTERSECT",EDGE,{"derivedFrom":[makeQuery(id+"F1.opRevolve","SWEPT_FACE",FACE,{"disambiguationData":[OSD([sQuery(id+"F0.wireOp",EDGE,"E14")])]}),makeQuery(id+"F5.opExtrude","SWEPT_FACE",FACE,{"disambiguationData":[OSD([sQuery(id+"F2.wireOp",EDGE,"E24")])]})]});
            var Q3;
            Q3=makeQuery(id+"F5.boolean.opBoolean","INTERSECT",EDGE,{"derivedFrom":[makeQuery(id+"F1.opRevolve","SWEPT_FACE",FACE,{"disambiguationData":[OSD([sQuery(id+"F0.wireOp",EDGE,"E14")])]}),makeQuery(id+"F5.opExtrude","SWEPT_FACE",FACE,{"disambiguationData":[OSD([sQuery(id+"F2.wireOp",EDGE,"E25.0.MirrorCS")])]})]});
            var Q4;
            Q4=makeQuery(id+"F5.boolean.opBoolean","INTERSECT",EDGE,{"derivedFrom":[makeQuery(id+"F1.opRevolve","SWEPT_FACE",FACE,{"disambiguationData":[OSD([sQuery(id+"F0.wireOp",EDGE,"E14")])]}),makeQuery(id+"F5.opExtrude","SWEPT_FACE",FACE,{"disambiguationData":[OSD([sQuery(id+"F2.wireOp",EDGE,"E26.4.0")])]})]});
            var Q5;
            Q5=makeQuery(id+"F5.boolean.opBoolean","INTERSECT",EDGE,{"derivedFrom":[makeQuery(id+"F1.opRevolve","SWEPT_FACE",FACE,{"disambiguationData":[OSD([sQuery(id+"F0.wireOp",EDGE,"E14")])]}),makeQuery(id+"F5.opExtrude","SWEPT_FACE",FACE,{"disambiguationData":[OSD([sQuery(id+"F2.wireOp",EDGE,"E26.4.1")])]})]});
            var Q6;
            Q6=makeQuery(id+"F5.boolean.opBoolean","INTERSECT",EDGE,{"derivedFrom":[makeQuery(id+"F1.opRevolve","SWEPT_FACE",FACE,{"disambiguationData":[OSD([sQuery(id+"F0.wireOp",EDGE,"E14")])]}),makeQuery(id+"F5.opExtrude","SWEPT_FACE",FACE,{"disambiguationData":[OSD([sQuery(id+"F2.wireOp",EDGE,"E26.3.0")])]})]});
            var Q7;
            Q7=makeQuery(id+"F5.boolean.opBoolean","INTERSECT",EDGE,{"derivedFrom":[makeQuery(id+"F1.opRevolve","SWEPT_FACE",FACE,{"disambiguationData":[OSD([sQuery(id+"F0.wireOp",EDGE,"E14")])]}),makeQuery(id+"F5.opExtrude","SWEPT_FACE",FACE,{"disambiguationData":[OSD([sQuery(id+"F2.wireOp",EDGE,"E26.3.1")])]})]});
            var Q8;
            Q8=makeQuery(id+"F5.boolean.opBoolean","INTERSECT",EDGE,{"derivedFrom":[makeQuery(id+"F1.opRevolve","SWEPT_FACE",FACE,{"disambiguationData":[OSD([sQuery(id+"F0.wireOp",EDGE,"E14")])]}),makeQuery(id+"F5.opExtrude","SWEPT_FACE",FACE,{"disambiguationData":[OSD([sQuery(id+"F2.wireOp",EDGE,"E26.2.0")])]})]});
            var Q9;
            Q9=makeQuery(id+"F5.boolean.opBoolean","INTERSECT",EDGE,{"derivedFrom":[makeQuery(id+"F1.opRevolve","SWEPT_FACE",FACE,{"disambiguationData":[OSD([sQuery(id+"F0.wireOp",EDGE,"E14")])]}),makeQuery(id+"F5.opExtrude","SWEPT_FACE",FACE,{"disambiguationData":[OSD([sQuery(id+"F2.wireOp",EDGE,"E26.2.1")])]})]});
            chamfer(context, id + "F10", {"entities" : qUnion([Q0, Q1, Q2, Q3, Q4, Q5, Q6, Q7, Q8, Q9]), "width" : 0.5 * mm, "tangentPropagation" : true});
        }
        {
            var Q0;
            Q0=makeQuery(id+"F6.boolean.opBoolean","COPY",EDGE,{"derivedFrom":makeQuery(id+"F6.opExtrude","CAP_EDGE",EDGE,{"disambiguationData":[OSD([sQuery(id+"F3.wireOp",EDGE,"E34.1.1")])],"isStart":false})});
            var Q1;
            Q1=makeQuery(id+"F6.boolean.opBoolean","COPY",EDGE,{"derivedFrom":makeQuery(id+"F6.opExtrude","CAP_EDGE",EDGE,{"disambiguationData":[OSD([sQuery(id+"F3.wireOp",EDGE,"E34.1.0")])],"isStart":false})});
            var Q2;
            Q2=makeQuery(id+"F6.boolean.opBoolean","COPY",EDGE,{"derivedFrom":makeQuery(id+"F6.opExtrude","CAP_EDGE",EDGE,{"disambiguationData":[OSD([sQuery(id+"F3.wireOp",EDGE,"E34.2.1")])],"isStart":false})});
            var Q3;
            Q3=makeQuery(id+"F6.boolean.opBoolean","COPY",EDGE,{"derivedFrom":makeQuery(id+"F6.opExtrude","CAP_EDGE",EDGE,{"disambiguationData":[OSD([sQuery(id+"F3.wireOp",EDGE,"E34.2.0")])],"isStart":false})});
            var Q4;
            Q4=makeQuery(id+"F6.boolean.opBoolean","COPY",EDGE,{"derivedFrom":makeQuery(id+"F6.opExtrude","CAP_EDGE",EDGE,{"disambiguationData":[OSD([sQuery(id+"F3.wireOp",EDGE,"E34.3.1")])],"isStart":false})});
            var Q5;
            {var subQ0=sQuery(id+"F0.wireOp",EDGE,"E2");var subQ1=sQuery(id+"F0.wireOp",EDGE,"E3");var subQ3=sQuery(id+"F3.wireOp",EDGE,"E34.2.0");Q5=makeQuery(id+"F6.boolean.opBoolean","SPLIT",EDGE,{"disambiguationData":[TD([makeQuery(id+"F6.opExtrude","SWEPT_FACE",FACE,{"disambiguationData":[OSD([subQ3])]})])],"derivedFrom":makeQuery(id+"F1.opRevolve","SWEPT_EDGE",EDGE,{"disambiguationData":[OSD([subQ0,subQ1])]})});}
            var Q6;
            {var subQ0=sQuery(id+"F0.wireOp",EDGE,"E2");var subQ1=sQuery(id+"F0.wireOp",EDGE,"E3");var subQ3=sQuery(id+"F3.wireOp",EDGE,"E34.1.0");Q6=makeQuery(id+"F6.boolean.opBoolean","SPLIT",EDGE,{"disambiguationData":[TD([makeQuery(id+"F6.opExtrude","SWEPT_FACE",FACE,{"disambiguationData":[OSD([subQ3])]})])],"derivedFrom":makeQuery(id+"F1.opRevolve","SWEPT_EDGE",EDGE,{"disambiguationData":[OSD([subQ0,subQ1])]})});}
            var Q7;
            Q7=makeQuery(id+"F6.boolean.opBoolean","COPY",EDGE,{"derivedFrom":makeQuery(id+"F6.opExtrude","CAP_EDGE",EDGE,{"disambiguationData":[OSD([sQuery(id+"F3.wireOp",EDGE,"E34.3.0")])],"isStart":false})});
            var Q8;
            {var subQ0=sQuery(id+"F0.wireOp",EDGE,"E2");var subQ1=sQuery(id+"F0.wireOp",EDGE,"E3");var subQ6=sQuery(id+"F3.wireOp",EDGE,"E34.3.0");Q8=makeQuery(id+"F6.boolean.opBoolean","SPLIT",EDGE,{"disambiguationData":[TD([makeQuery(id+"F6.opExtrude","SWEPT_FACE",FACE,{"disambiguationData":[OSD([subQ6])]})])],"derivedFrom":makeQuery(id+"F1.opRevolve","SWEPT_EDGE",EDGE,{"disambiguationData":[OSD([subQ0,subQ1])]})});}
            var Q9;
            Q9=makeQuery(id+"F6.boolean.opBoolean","COPY",EDGE,{"derivedFrom":makeQuery(id+"F6.opExtrude","CAP_EDGE",EDGE,{"disambiguationData":[OSD([sQuery(id+"F3.wireOp",EDGE,"E34.4.1")])],"isStart":false})});
            var Q10;
            Q10=makeQuery(id+"F6.boolean.opBoolean","COPY",EDGE,{"derivedFrom":makeQuery(id+"F6.opExtrude","CAP_EDGE",EDGE,{"disambiguationData":[OSD([sQuery(id+"F3.wireOp",EDGE,"E34.4.0")])],"isStart":false})});
            var Q11;
            {var subQ0=sQuery(id+"F0.wireOp",EDGE,"E2");var subQ1=sQuery(id+"F0.wireOp",EDGE,"E3");var subQ3=sQuery(id+"F3.wireOp",EDGE,"E34.4.0");Q11=makeQuery(id+"F6.boolean.opBoolean","SPLIT",EDGE,{"disambiguationData":[TD([makeQuery(id+"F6.opExtrude","SWEPT_FACE",FACE,{"disambiguationData":[OSD([subQ3])]})])],"derivedFrom":makeQuery(id+"F1.opRevolve","SWEPT_EDGE",EDGE,{"disambiguationData":[OSD([subQ0,subQ1])]})});}
            var Q12;
            Q12=makeQuery(id+"F6.boolean.opBoolean","COPY",EDGE,{"derivedFrom":makeQuery(id+"F6.opExtrude","CAP_EDGE",EDGE,{"disambiguationData":[OSD([sQuery(id+"F3.wireOp",EDGE,"E34.5.1")])],"isStart":false})});
            var Q13;
            Q13=makeQuery(id+"F6.boolean.opBoolean","COPY",EDGE,{"derivedFrom":makeQuery(id+"F6.opExtrude","CAP_EDGE",EDGE,{"disambiguationData":[OSD([sQuery(id+"F3.wireOp",EDGE,"E34.5.0")])],"isStart":false})});
            var Q14;
            {var subQ0=sQuery(id+"F0.wireOp",EDGE,"E2");var subQ1=sQuery(id+"F0.wireOp",EDGE,"E3");var subQ2=sQuery(id+"F3.wireOp",EDGE,"E34.5.0");Q14=makeQuery(id+"F6.boolean.opBoolean","SPLIT",EDGE,{"disambiguationData":[TD([makeQuery(id+"F6.opExtrude","SWEPT_FACE",FACE,{"disambiguationData":[OSD([subQ2])]})])],"derivedFrom":makeQuery(id+"F1.opRevolve","SWEPT_EDGE",EDGE,{"disambiguationData":[OSD([subQ0,subQ1])]})});}
            var Q15;
            Q15=makeQuery(id+"F6.boolean.opBoolean","COPY",EDGE,{"derivedFrom":makeQuery(id+"F6.opExtrude","CAP_EDGE",EDGE,{"disambiguationData":[OSD([sQuery(id+"F3.wireOp",EDGE,"E34.6.1")])],"isStart":false})});
            var Q16;
            Q16=makeQuery(id+"F6.boolean.opBoolean","COPY",EDGE,{"derivedFrom":makeQuery(id+"F6.opExtrude","CAP_EDGE",EDGE,{"disambiguationData":[OSD([sQuery(id+"F3.wireOp",EDGE,"E34.6.0")])],"isStart":false})});
            var Q17;
            {var subQ0=sQuery(id+"F0.wireOp",EDGE,"E2");var subQ1=sQuery(id+"F0.wireOp",EDGE,"E3");var subQ6=sQuery(id+"F3.wireOp",EDGE,"E34.6.0");Q17=makeQuery(id+"F6.boolean.opBoolean","SPLIT",EDGE,{"disambiguationData":[TD([makeQuery(id+"F6.opExtrude","SWEPT_FACE",FACE,{"disambiguationData":[OSD([subQ6])]})])],"derivedFrom":makeQuery(id+"F1.opRevolve","SWEPT_EDGE",EDGE,{"disambiguationData":[OSD([subQ0,subQ1])]})});}
            var Q18;
            Q18=makeQuery(id+"F6.boolean.opBoolean","COPY",EDGE,{"derivedFrom":makeQuery(id+"F6.opExtrude","CAP_EDGE",EDGE,{"disambiguationData":[OSD([sQuery(id+"F3.wireOp",EDGE,"E34.7.1")])],"isStart":false})});
            var Q19;
            Q19=makeQuery(id+"F6.boolean.opBoolean","COPY",EDGE,{"derivedFrom":makeQuery(id+"F6.opExtrude","CAP_EDGE",EDGE,{"disambiguationData":[OSD([sQuery(id+"F3.wireOp",EDGE,"E34.7.0")])],"isStart":false})});
            var Q20;
            {var subQ0=sQuery(id+"F0.wireOp",EDGE,"E2");var subQ1=sQuery(id+"F0.wireOp",EDGE,"E3");var subQ3=sQuery(id+"F3.wireOp",EDGE,"E34.7.0");Q20=makeQuery(id+"F6.boolean.opBoolean","SPLIT",EDGE,{"disambiguationData":[TD([makeQuery(id+"F6.opExtrude","SWEPT_FACE",FACE,{"disambiguationData":[OSD([subQ3])]})])],"derivedFrom":makeQuery(id+"F1.opRevolve","SWEPT_EDGE",EDGE,{"disambiguationData":[OSD([subQ0,subQ1])]})});}
            var Q21;
            Q21=makeQuery(id+"F6.boolean.opBoolean","COPY",EDGE,{"derivedFrom":makeQuery(id+"F6.opExtrude","CAP_EDGE",EDGE,{"disambiguationData":[OSD([sQuery(id+"F3.wireOp",EDGE,"E34.8.1")])],"isStart":false})});
            var Q22;
            Q22=makeQuery(id+"F6.boolean.opBoolean","COPY",EDGE,{"derivedFrom":makeQuery(id+"F6.opExtrude","CAP_EDGE",EDGE,{"disambiguationData":[OSD([sQuery(id+"F3.wireOp",EDGE,"E34.8.0")])],"isStart":false})});
            var Q23;
            {var subQ0=sQuery(id+"F0.wireOp",EDGE,"E2");var subQ1=sQuery(id+"F0.wireOp",EDGE,"E3");var subQ3=sQuery(id+"F3.wireOp",EDGE,"E34.8.0");Q23=makeQuery(id+"F6.boolean.opBoolean","SPLIT",EDGE,{"disambiguationData":[TD([makeQuery(id+"F6.opExtrude","SWEPT_FACE",FACE,{"disambiguationData":[OSD([subQ3])]})])],"derivedFrom":makeQuery(id+"F1.opRevolve","SWEPT_EDGE",EDGE,{"disambiguationData":[OSD([subQ0,subQ1])]})});}
            var Q24;
            Q24=makeQuery(id+"F6.boolean.opBoolean","COPY",EDGE,{"derivedFrom":makeQuery(id+"F6.opExtrude","CAP_EDGE",EDGE,{"disambiguationData":[OSD([sQuery(id+"F3.wireOp",EDGE,"E34.9.1")])],"isStart":false})});
            var Q25;
            {var subQ0=sQuery(id+"F0.wireOp",EDGE,"E2");var subQ1=sQuery(id+"F0.wireOp",EDGE,"E3");var subQ4=sQuery(id+"F3.wireOp",EDGE,"E33.0.MirrorCS");Q25=makeQuery(id+"F6.boolean.opBoolean","SPLIT",EDGE,{"disambiguationData":[TD([makeQuery(id+"F6.opExtrude","SWEPT_FACE",FACE,{"disambiguationData":[OSD([subQ4])]})])],"derivedFrom":makeQuery(id+"F1.opRevolve","SWEPT_EDGE",EDGE,{"disambiguationData":[OSD([subQ0,subQ1])]})});}
            var Q26;
            Q26=makeQuery(id+"F6.boolean.opBoolean","COPY",EDGE,{"derivedFrom":makeQuery(id+"F6.opExtrude","CAP_EDGE",EDGE,{"disambiguationData":[OSD([sQuery(id+"F3.wireOp",EDGE,"E33.0.MirrorCS")])],"isStart":false})});
            var Q27;
            Q27=makeQuery(id+"F6.boolean.opBoolean","COPY",EDGE,{"derivedFrom":makeQuery(id+"F6.opExtrude","CAP_EDGE",EDGE,{"disambiguationData":[OSD([sQuery(id+"F3.wireOp",EDGE,"E34.9.0")])],"isStart":false})});
            var Q28;
            Q28=makeQuery(id+"F6.boolean.opBoolean","COPY",EDGE,{"derivedFrom":makeQuery(id+"F6.opExtrude","CAP_EDGE",EDGE,{"disambiguationData":[OSD([sQuery(id+"F3.wireOp",EDGE,"E32")])],"isStart":false})});
            var Q29;
            {var subQ0=sQuery(id+"F0.wireOp",EDGE,"E2");var subQ1=sQuery(id+"F0.wireOp",EDGE,"E3");var subQ5=sQuery(id+"F3.wireOp",EDGE,"E32");Q29=makeQuery(id+"F6.boolean.opBoolean","SPLIT",EDGE,{"disambiguationData":[TD([makeQuery(id+"F6.opExtrude","SWEPT_FACE",FACE,{"disambiguationData":[OSD([subQ5])]})])],"derivedFrom":makeQuery(id+"F1.opRevolve","SWEPT_EDGE",EDGE,{"disambiguationData":[OSD([subQ0,subQ1])]})});}
            var Q30;
            Q30=makeQuery(id+"F6.boolean.opBoolean","COPY",EDGE,{"derivedFrom":makeQuery(id+"F6.opExtrude","CAP_EDGE",EDGE,{"disambiguationData":[OSD([sQuery(id+"F3.wireOp",EDGE,"E34.3.0")])],"isStart":true})});
            var Q31;
            Q31=makeQuery(id+"F6.boolean.opBoolean","COPY",EDGE,{"derivedFrom":makeQuery(id+"F6.opExtrude","CAP_EDGE",EDGE,{"disambiguationData":[OSD([sQuery(id+"F3.wireOp",EDGE,"E34.4.1")])],"isStart":true})});
            var Q32;
            Q32=makeQuery(id+"F6.boolean.opBoolean","COPY",EDGE,{"derivedFrom":makeQuery(id+"F6.opExtrude","CAP_EDGE",EDGE,{"disambiguationData":[OSD([sQuery(id+"F3.wireOp",EDGE,"E34.3.1")])],"isStart":true})});
            var Q33;
            Q33=makeQuery(id+"F6.boolean.opBoolean","COPY",EDGE,{"derivedFrom":makeQuery(id+"F6.opExtrude","CAP_EDGE",EDGE,{"disambiguationData":[OSD([sQuery(id+"F3.wireOp",EDGE,"E34.2.0")])],"isStart":true})});
            var Q34;
            Q34=makeQuery(id+"F6.boolean.opBoolean","COPY",EDGE,{"derivedFrom":makeQuery(id+"F6.opExtrude","CAP_EDGE",EDGE,{"disambiguationData":[OSD([sQuery(id+"F3.wireOp",EDGE,"E34.2.1")])],"isStart":true})});
            var Q35;
            Q35=makeQuery(id+"F6.boolean.opBoolean","COPY",EDGE,{"derivedFrom":makeQuery(id+"F6.opExtrude","CAP_EDGE",EDGE,{"disambiguationData":[OSD([sQuery(id+"F3.wireOp",EDGE,"E34.1.0")])],"isStart":true})});
            var Q36;
            Q36=makeQuery(id+"F6.boolean.opBoolean","COPY",EDGE,{"derivedFrom":makeQuery(id+"F6.opExtrude","CAP_EDGE",EDGE,{"disambiguationData":[OSD([sQuery(id+"F3.wireOp",EDGE,"E34.1.1")])],"isStart":true})});
            var Q37;
            Q37=makeQuery(id+"F6.boolean.opBoolean","COPY",EDGE,{"derivedFrom":makeQuery(id+"F6.opExtrude","CAP_EDGE",EDGE,{"disambiguationData":[OSD([sQuery(id+"F3.wireOp",EDGE,"E32")])],"isStart":true})});
            var Q38;
            Q38=makeQuery(id+"F6.boolean.opBoolean","COPY",EDGE,{"derivedFrom":makeQuery(id+"F6.opExtrude","CAP_EDGE",EDGE,{"disambiguationData":[OSD([sQuery(id+"F3.wireOp",EDGE,"E33.0.MirrorCS")])],"isStart":true})});
            var Q39;
            Q39=makeQuery(id+"F6.boolean.opBoolean","COPY",EDGE,{"derivedFrom":makeQuery(id+"F6.opExtrude","CAP_EDGE",EDGE,{"disambiguationData":[OSD([sQuery(id+"F3.wireOp",EDGE,"E34.9.0")])],"isStart":true})});
            var Q40;
            Q40=makeQuery(id+"F6.boolean.opBoolean","COPY",EDGE,{"derivedFrom":makeQuery(id+"F6.opExtrude","CAP_EDGE",EDGE,{"disambiguationData":[OSD([sQuery(id+"F3.wireOp",EDGE,"E34.9.1")])],"isStart":true})});
            var Q41;
            Q41=makeQuery(id+"F6.boolean.opBoolean","COPY",EDGE,{"derivedFrom":makeQuery(id+"F6.opExtrude","CAP_EDGE",EDGE,{"disambiguationData":[OSD([sQuery(id+"F3.wireOp",EDGE,"E34.8.0")])],"isStart":true})});
            var Q42;
            Q42=makeQuery(id+"F6.boolean.opBoolean","COPY",EDGE,{"derivedFrom":makeQuery(id+"F6.opExtrude","CAP_EDGE",EDGE,{"disambiguationData":[OSD([sQuery(id+"F3.wireOp",EDGE,"E34.8.1")])],"isStart":true})});
            var Q43;
            Q43=makeQuery(id+"F6.boolean.opBoolean","COPY",EDGE,{"derivedFrom":makeQuery(id+"F6.opExtrude","CAP_EDGE",EDGE,{"disambiguationData":[OSD([sQuery(id+"F3.wireOp",EDGE,"E34.7.0")])],"isStart":true})});
            var Q44;
            Q44=makeQuery(id+"F6.boolean.opBoolean","COPY",EDGE,{"derivedFrom":makeQuery(id+"F6.opExtrude","CAP_EDGE",EDGE,{"disambiguationData":[OSD([sQuery(id+"F3.wireOp",EDGE,"E34.7.1")])],"isStart":true})});
            var Q45;
            Q45=makeQuery(id+"F6.boolean.opBoolean","COPY",EDGE,{"derivedFrom":makeQuery(id+"F6.opExtrude","CAP_EDGE",EDGE,{"disambiguationData":[OSD([sQuery(id+"F3.wireOp",EDGE,"E34.6.0")])],"isStart":true})});
            var Q46;
            Q46=makeQuery(id+"F6.boolean.opBoolean","COPY",EDGE,{"derivedFrom":makeQuery(id+"F6.opExtrude","CAP_EDGE",EDGE,{"disambiguationData":[OSD([sQuery(id+"F3.wireOp",EDGE,"E34.6.1")])],"isStart":true})});
            var Q47;
            Q47=makeQuery(id+"F6.boolean.opBoolean","COPY",EDGE,{"derivedFrom":makeQuery(id+"F6.opExtrude","CAP_EDGE",EDGE,{"disambiguationData":[OSD([sQuery(id+"F3.wireOp",EDGE,"E34.5.0")])],"isStart":true})});
            var Q48;
            Q48=makeQuery(id+"F6.boolean.opBoolean","COPY",EDGE,{"derivedFrom":makeQuery(id+"F6.opExtrude","CAP_EDGE",EDGE,{"disambiguationData":[OSD([sQuery(id+"F3.wireOp",EDGE,"E34.5.1")])],"isStart":true})});
            var Q49;
            Q49=makeQuery(id+"F6.boolean.opBoolean","COPY",EDGE,{"derivedFrom":makeQuery(id+"F6.opExtrude","CAP_EDGE",EDGE,{"disambiguationData":[OSD([sQuery(id+"F3.wireOp",EDGE,"E34.4.0")])],"isStart":true})});
            fillet(context, id + "F11", {"entities" : qUnion([Q0, Q1, Q2, Q3, Q4, Q5, Q6, Q7, Q8, Q9, Q10, Q11, Q12, Q13, Q14, Q15, Q16, Q17, Q18, Q19, Q20, Q21, Q22, Q23, Q24, Q25, Q26, Q27, Q28, Q29, Q30, Q31, Q32, Q33, Q34, Q35, Q36, Q37, Q38, Q39, Q40, Q41, Q42, Q43, Q44, Q45, Q46, Q47, Q48, Q49]), "radius" : 1.5 * mm, "tangentPropagation" : true, "allowEdgeOverflow" : false});
        }
        {
            var Q0;
            Q0=makeQuery(id+"F1.opRevolve","SWEPT_FACE",FACE,{"disambiguationData":[OSD([sQuery(id+"F0.wireOp",EDGE,"E4")])]});
            var sketch = newSketch(context, id + "F12", { "sketchPlane" : qUnion([Q0])});
            skCircle(sketch, "E35", {"center": v(0, 0) * mm, "radius": 5 * mm});
            skSolve(sketch);
        }
        {
            var Q0;
            Q0=makeQuery(id+"F12.imprint","IMPRINT",FACE,{"disambiguationData":[TD([[makeQuery(id+"F12.imprint","IMPRINT",EDGE,{"derivedFrom":sQuery(id+"F12.wireOp",EDGE,"E35")}),1.0]])]});
            extrude(context, id + "F13", {"entities" : qUnion([Q0]), "depth" : 25 * mm, "hasSecondDirection" : true, "secondDirectionOppositeDirection" : true, "secondDirectionDepth" : 125 * mm});
        }
    });
